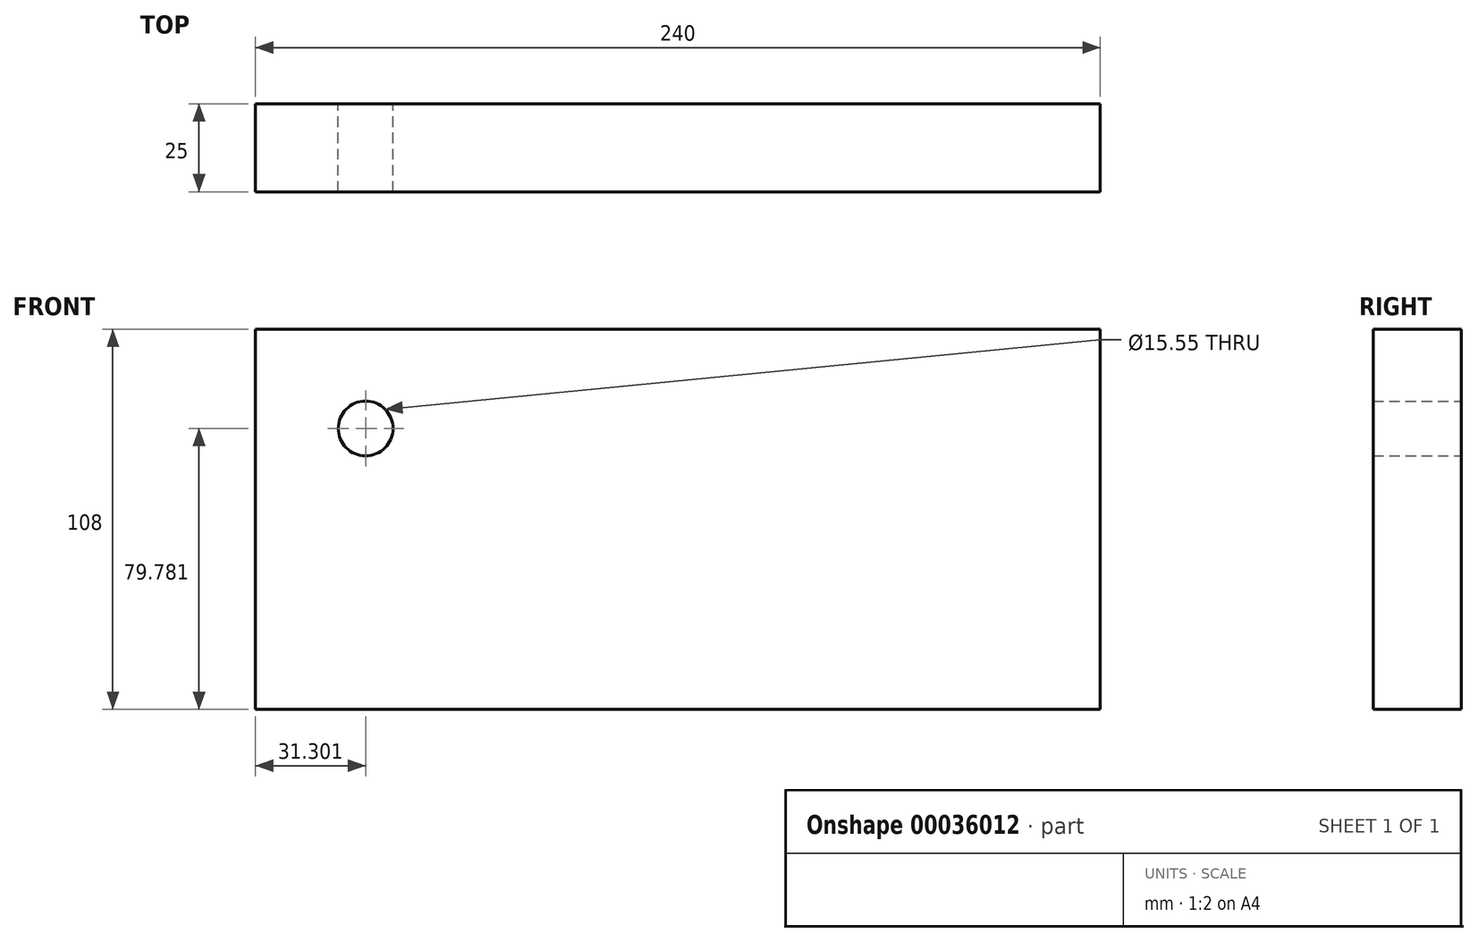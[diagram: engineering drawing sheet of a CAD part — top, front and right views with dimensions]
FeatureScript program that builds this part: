
annotation { "Feature Type Name" : "Feature", "Feature Type Description" : "" }
export const myFeature = defineFeature(function(context is Context, id is Id, definition is map)
    precondition{}
    {
        {
            var Q0;
            Q0=qCreatedBy(makeId("Front.planeOp"),FACE);
            var sketch = newSketch(context, id + "F0", { "sketchPlane" : qUnion([Q0])});
            skLineSegment(sketch, "E0.bottom", {"start": v(-132.5, 47.18) * mm, "end": v(107.5, 47.18) * mm});
            skLineSegment(sketch, "E0.top", {"start": v(-132.5, -60.82) * mm, "end": v(107.5, -60.82) * mm});
            skLineSegment(sketch, "E0.left", {"start": v(-132.5, 47.18) * mm, "end": v(-132.5, -60.82) * mm});
            skLineSegment(sketch, "E0.right", {"start": v(107.5, 47.18) * mm, "end": v(107.5, -60.82) * mm});
            skCircle(sketch, "E1", {"center": v(-101.2, 18.96) * mm, "radius": 7.77 * mm});
            skSolve(sketch);
        }
        {
            var Q0;
            Q0=makeQuery(id+"F0.imprint","IMPRINT",FACE,{"disambiguationData":[TD([[makeQuery(id+"F0.imprint","IMPRINT",EDGE,{"derivedFrom":sQuery(id+"F0.wireOp",EDGE,"E0.bottom")}),-1.0]])]});
            extrude(context, id + "F1", {"entities" : qUnion([Q0]), "depth" : 25 * mm});
        }
    });
